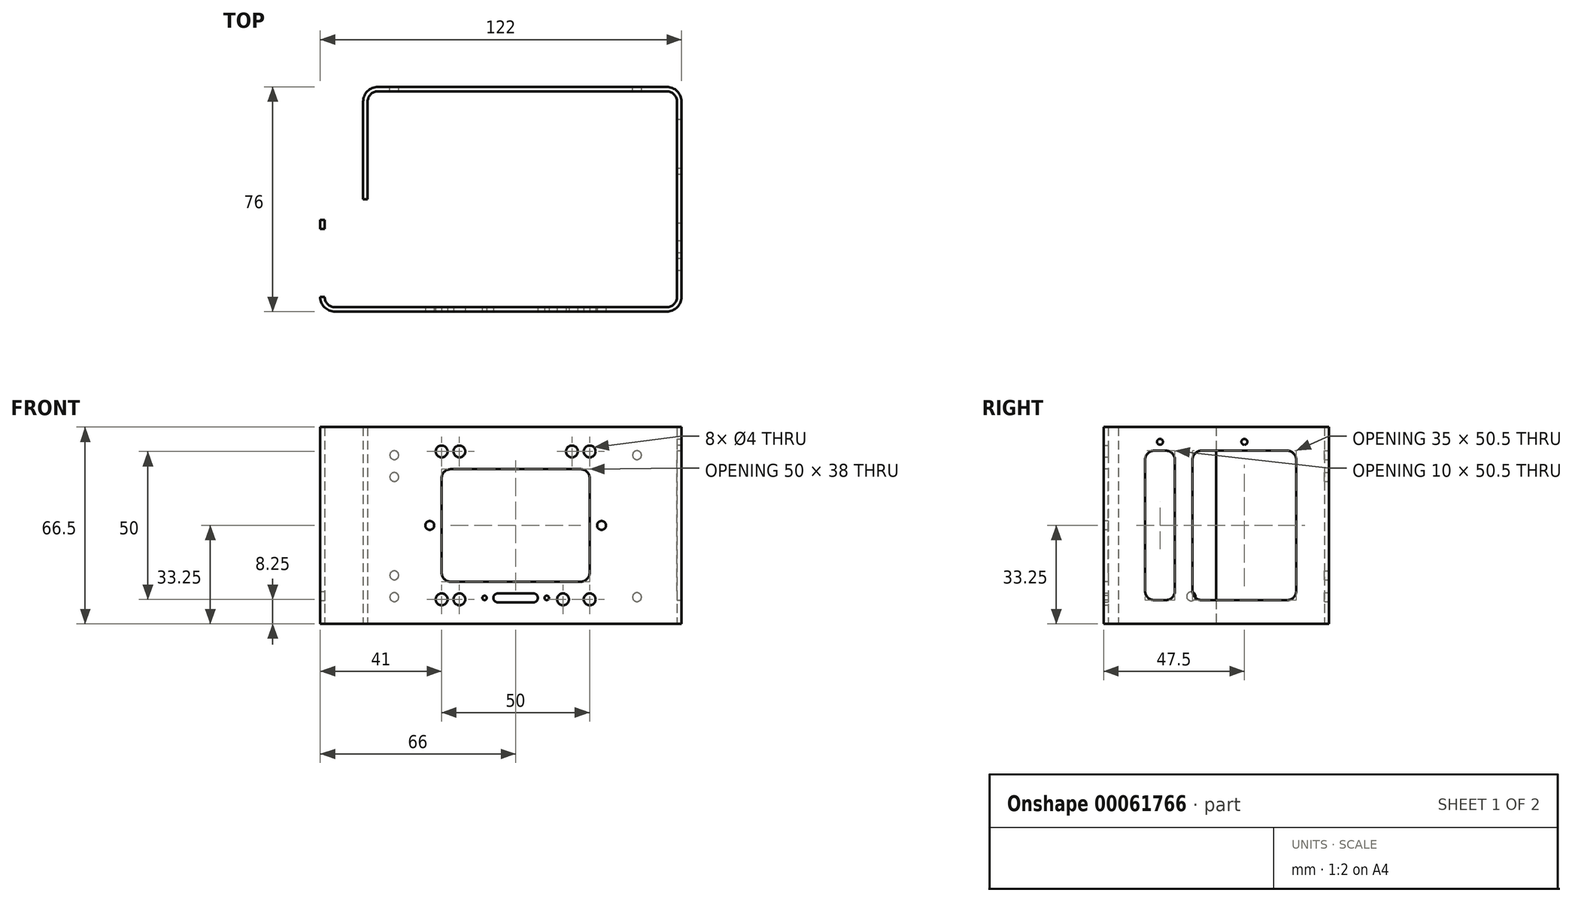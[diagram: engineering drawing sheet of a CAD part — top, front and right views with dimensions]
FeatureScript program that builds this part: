
annotation { "Feature Type Name" : "Feature", "Feature Type Description" : "" }
export const myFeature = defineFeature(function(context is Context, id is Id, definition is map)
    precondition{}
    {
        {
            var Q0;
            Q0=qCreatedBy(makeId("Top.planeOp"),FACE);
            var sketch = newSketch(context, id + "F0", { "sketchPlane" : qUnion([Q0])});
            skLineSegment(sketch, "E0", {"start": v(-64.5, 33) * mm, "end": v(-64.5, -33) * mm});
            skLineSegment(sketch, "E1", {"start": v(-61, -36.5) * mm, "end": v(51, -36.5) * mm});
            skLineSegment(sketch, "E2", {"start": v(54.5, -33) * mm, "end": v(54.5, 33) * mm});
            skLineSegment(sketch, "E3", {"start": v(51, 36.5) * mm, "end": v(-46.5, 36.5) * mm});
            skLineSegment(sketch, "E4", {"start": v(-50, 33) * mm, "end": v(-50, 0) * mm});
            skLineSegment(sketch, "E5.0", {"start": v(-51.5, 33) * mm, "end": v(-51.5, 0) * mm});
            skLineSegment(sketch, "E5.1", {"start": v(-66, 33) * mm, "end": v(-66, -33) * mm});
            skLineSegment(sketch, "E5.2", {"start": v(-61, -38) * mm, "end": v(51, -38) * mm});
            skLineSegment(sketch, "E5.3", {"start": v(56, -33) * mm, "end": v(56, 33) * mm});
            skLineSegment(sketch, "E5.4", {"start": v(51, 38) * mm, "end": v(-46.5, 38) * mm});
            skLineSegment(sketch, "E6", {"start": v(-50, 0) * mm, "end": v(-51.5, 0) * mm});
            skLineSegment(sketch, "E7", {"start": v(-64.5, 33) * mm, "end": v(-66, 33) * mm});
            skPoint(sketch, "E8.visualSharp", {"position": v(-64.5, -36.5) * mm});
            skArc(sketch, "E8.filletArc", {"start": v(-64.5, -33) * mm, "mid": v(-63.47, -35.47) * mm, "end": v(-61, -36.5) * mm});
            skPoint(sketch, "E9.visualSharp", {"position": v(54.5, -36.5) * mm});
            skArc(sketch, "E9.filletArc", {"start": v(51, -36.5) * mm, "mid": v(53.47, -35.47) * mm, "end": v(54.5, -33) * mm});
            skPoint(sketch, "E10.visualSharp", {"position": v(54.5, 36.5) * mm});
            skArc(sketch, "E10.filletArc", {"start": v(54.5, 33) * mm, "mid": v(53.47, 35.47) * mm, "end": v(51, 36.5) * mm});
            skPoint(sketch, "E11.visualSharp", {"position": v(-50, 36.5) * mm});
            skArc(sketch, "E11.filletArc", {"start": v(-46.5, 36.5) * mm, "mid": v(-48.97, 35.47) * mm, "end": v(-50, 33) * mm});
            skPoint(sketch, "E12.visualSharp", {"position": v(-66, -38) * mm});
            skArc(sketch, "E12.filletArc", {"start": v(-66, -33) * mm, "mid": v(-64.54, -36.54) * mm, "end": v(-61, -38) * mm});
            skPoint(sketch, "E13.visualSharp", {"position": v(56, -38) * mm});
            skArc(sketch, "E13.filletArc", {"start": v(51, -38) * mm, "mid": v(54.54, -36.54) * mm, "end": v(56, -33) * mm});
            skPoint(sketch, "E14.visualSharp", {"position": v(56, 38) * mm});
            skArc(sketch, "E14.filletArc", {"start": v(56, 33) * mm, "mid": v(54.54, 36.54) * mm, "end": v(51, 38) * mm});
            skPoint(sketch, "E15.visualSharp", {"position": v(-51.5, 38) * mm});
            skArc(sketch, "E15.filletArc", {"start": v(-46.5, 38) * mm, "mid": v(-50.04, 36.54) * mm, "end": v(-51.5, 33) * mm});
            skLineSegment(sketch, "E16", {"start": v(54.5, 0) * mm, "end": v(-12.48, 0) * mm, "construction": true});
            skLineSegment(sketch, "E17", {"start": v(2.25, 36.5) * mm, "end": v(-0.93, -15.16) * mm, "construction": true});
            skSolve(sketch);
        }
        {
            var Q0;
            Q0=qSketchRegion(id+"F0",true);
            extrude(context, id + "F1", {"entities" : qUnion([Q0]), "depth" : 66.5 * mm});
        }
        {
            var Q0;
            Q0=makeQuery(id+"F1.opExtrude","SWEPT_FACE",FACE,{"disambiguationData":[OSD([sQuery(id+"F0.wireOp",EDGE,"E5.2")])]});
            var sketch = newSketch(context, id + "F2", { "sketchPlane" : qUnion([Q0])});
            skLineSegment(sketch, "E18.bottom", {"start": v(-22, 52.25) * mm, "end": v(22, 52.25) * mm});
            skLineSegment(sketch, "E18.top", {"start": v(-22, 14.25) * mm, "end": v(22, 14.25) * mm});
            skLineSegment(sketch, "E18.left", {"start": v(-25, 49.25) * mm, "end": v(-25, 17.25) * mm});
            skLineSegment(sketch, "E18.right", {"start": v(25, 49.25) * mm, "end": v(25, 17.25) * mm});
            skLineSegment(sketch, "E19", {"start": v(-61, 33.25) * mm, "end": v(46, 33.25) * mm, "construction": true});
            skLineSegment(sketch, "E20", {"start": v(25, 33.25) * mm, "end": v(-25, 33.25) * mm, "construction": true});
            skPoint(sketch, "E21.visualSharp", {"position": v(-25, 52.25) * mm});
            skArc(sketch, "E21.filletArc", {"start": v(-22, 52.25) * mm, "mid": v(-24.12, 51.37) * mm, "end": v(-25, 49.25) * mm});
            skPoint(sketch, "E22.visualSharp", {"position": v(25, 52.25) * mm});
            skArc(sketch, "E22.filletArc", {"start": v(25, 49.25) * mm, "mid": v(24.12, 51.37) * mm, "end": v(22, 52.25) * mm});
            skPoint(sketch, "E23.visualSharp", {"position": v(25, 14.25) * mm});
            skArc(sketch, "E23.filletArc", {"start": v(22, 14.25) * mm, "mid": v(24.12, 15.13) * mm, "end": v(25, 17.25) * mm});
            skPoint(sketch, "E24.visualSharp", {"position": v(-25, 14.25) * mm});
            skArc(sketch, "E24.filletArc", {"start": v(-25, 17.25) * mm, "mid": v(-24.12, 15.13) * mm, "end": v(-22, 14.25) * mm});
            skCircle(sketch, "E25", {"center": v(-29, 33.25) * mm, "radius": 1.5 * mm});
            skCircle(sketch, "E26.MirrorC", {"center": v(29, 33.25) * mm, "radius": 1.5 * mm});
            skCircle(sketch, "E27", {"center": v(-25, 58.25) * mm, "radius": 2 * mm});
            skCircle(sketch, "E28.MirrorC", {"center": v(25, 58.25) * mm, "radius": 2 * mm});
            skCircle(sketch, "E29.MirrorC", {"center": v(-25, 8.25) * mm, "radius": 2 * mm});
            skCircle(sketch, "E30.MirrorC", {"center": v(25, 8.25) * mm, "radius": 2 * mm});
            skLineSegment(sketch, "E31.bottom", {"start": v(-6, 7.25) * mm, "end": v(6, 7.25) * mm});
            skPoint(sketch, "E32.visualSharp", {"position": v(7.5, 10.25) * mm});
            skLineSegment(sketch, "E31.top", {"start": v(-6, 10.25) * mm, "end": v(6, 10.25) * mm});
            skArc(sketch, "E33.filletArc", {"start": v(-6, 10.25) * mm, "mid": v(-7.06, 9.81) * mm, "end": v(-7.5, 8.75) * mm});
            skLineSegment(sketch, "E31.left", {"start": v(-7.5, 8.75) * mm, "end": v(-7.5, 8.75) * mm});
            skLineSegment(sketch, "E31.right", {"start": v(7.5, 8.75) * mm, "end": v(7.5, 8.75) * mm});
            skArc(sketch, "E34.filletArc", {"start": v(-7.5, 8.75) * mm, "mid": v(-7.06, 7.69) * mm, "end": v(-6, 7.25) * mm});
            skArc(sketch, "E35.filletArc", {"start": v(6, 7.25) * mm, "mid": v(7.06, 7.69) * mm, "end": v(7.5, 8.75) * mm});
            skArc(sketch, "E32.filletArc", {"start": v(7.5, 8.75) * mm, "mid": v(7.06, 9.81) * mm, "end": v(6, 10.25) * mm});
            skCircle(sketch, "E36", {"center": v(-10.5, 8.75) * mm, "radius": 0.75 * mm});
            skPoint(sketch, "E37", {"position": v(0, 10.25) * mm});
            skLineSegment(sketch, "E38", {"start": v(-10.5, 8.75) * mm, "end": v(8.14, 8.75) * mm, "construction": true});
            skPoint(sketch, "E33.visualSharp", {"position": v(-7.5, 10.25) * mm});
            skPoint(sketch, "E34.visualSharp", {"position": v(-7.5, 7.25) * mm});
            skPoint(sketch, "E35.visualSharp", {"position": v(7.5, 7.25) * mm});
            skLineSegment(sketch, "E39", {"start": v(0, 10.25) * mm, "end": v(0, 7.25) * mm, "construction": true});
            skCircle(sketch, "E40.MirrorC", {"center": v(10.5, 8.75) * mm, "radius": 0.75 * mm});
            skLineSegment(sketch, "E41", {"start": v(-25, 8.25) * mm, "end": v(-25, 58.25) * mm, "construction": true});
            skLineSegment(sketch, "E42", {"start": v(25, 58.25) * mm, "end": v(25, 8.25) * mm, "construction": true});
            skLineSegment(sketch, "E43", {"start": v(-25, 8.25) * mm, "end": v(25, 8.25) * mm, "construction": true});
            skLineSegment(sketch, "E44", {"start": v(25, 58.25) * mm, "end": v(-25, 58.25) * mm, "construction": true});
            skCircle(sketch, "E45", {"center": v(-19, 8.25) * mm, "radius": 2 * mm});
            skCircle(sketch, "E46.MirrorC", {"center": v(-19, 58.25) * mm, "radius": 2 * mm});
            skCircle(sketch, "E47.MirrorC", {"center": v(19, 58.25) * mm, "radius": 2 * mm});
            skCircle(sketch, "E48", {"center": v(16, 8.25) * mm, "radius": 2 * mm});
            skPoint(sketch, "E49", {"position": v(-61, 33.25) * mm});
            skSolve(sketch);
        }
        {
            var Q0;
            Q0 = qSketchRegion(id + "F2", true);
            extrude(context, id + "F3", {"entities" : qUnion([Q0]), "operationType" : NewBodyOperationType.REMOVE, "oppositeDirection" : true, "depth" : 25 * mm});
        }
        {
            var Q0;
            Q0=makeQuery(id+"F1.opExtrude","SWEPT_FACE",FACE,{"disambiguationData":[OSD([sQuery(id+"F0.wireOp",EDGE,"E5.4")])]});
            var sketch = newSketch(context, id + "F4", { "sketchPlane" : qUnion([Q0])});
            skCircle(sketch, "E50", {"center": v(-41, 57) * mm, "radius": 1.5 * mm});
            skLineSegment(sketch, "E51", {"start": v(-41, 57) * mm, "end": v(-41, 9) * mm, "construction": true});
            skLineSegment(sketch, "E52", {"start": v(-41, 9) * mm, "end": v(41, 9) * mm, "construction": true});
            skLineSegment(sketch, "E53", {"start": v(41, 9) * mm, "end": v(41, 57) * mm, "construction": true});
            skLineSegment(sketch, "E54", {"start": v(41, 57) * mm, "end": v(-41, 57) * mm, "construction": true});
            skCircle(sketch, "E55", {"center": v(-41, 9) * mm, "radius": 1.5 * mm});
            skCircle(sketch, "E56", {"center": v(41, 9) * mm, "radius": 1.5 * mm});
            skCircle(sketch, "E57", {"center": v(41, 57) * mm, "radius": 1.5 * mm});
            skLineSegment(sketch, "E58", {"start": v(0, 1) * mm, "end": v(0, 113) * mm, "construction": true});
            skPoint(sketch, "E58.endSnap0", {"position": v(0, 1) * mm});
            skPoint(sketch, "E59", {"position": v(0, 57) * mm});
            skCircle(sketch, "E60", {"center": v(41, 49.63) * mm, "radius": 1.5 * mm});
            skCircle(sketch, "E61", {"center": v(41, 16.38) * mm, "radius": 1.5 * mm});
            skLineSegment(sketch, "E62", {"start": v(33.74, 33) * mm, "end": v(24.94, 33) * mm, "construction": true});
            skSolve(sketch);
        }
        {
            var Q0;
            Q0=makeQuery(id+"F4.imprint","IMPRINT",FACE,{"disambiguationData":[TD([[makeQuery(id+"F4.imprint","IMPRINT",EDGE,{"derivedFrom":sQuery(id+"F4.wireOp",EDGE,"E50")}),1.0]])]});
            var Q1;
            Q1=makeQuery(id+"F4.imprint","IMPRINT",FACE,{"disambiguationData":[TD([[makeQuery(id+"F4.imprint","IMPRINT",EDGE,{"derivedFrom":sQuery(id+"F4.wireOp",EDGE,"E55")}),1.0]])]});
            var Q2;
            Q2=makeQuery(id+"F4.imprint","IMPRINT",FACE,{"disambiguationData":[TD([[makeQuery(id+"F4.imprint","IMPRINT",EDGE,{"derivedFrom":sQuery(id+"F4.wireOp",EDGE,"E56")}),1.0]])]});
            var Q3;
            Q3=makeQuery(id+"F4.imprint","IMPRINT",FACE,{"disambiguationData":[TD([[makeQuery(id+"F4.imprint","IMPRINT",EDGE,{"derivedFrom":sQuery(id+"F4.wireOp",EDGE,"E57")}),1.0]])]});
            var Q4;
            Q4=makeQuery(id+"F4.imprint","IMPRINT",FACE,{"disambiguationData":[TD([[makeQuery(id+"F4.imprint","IMPRINT",EDGE,{"derivedFrom":sQuery(id+"F4.wireOp",EDGE,"E61")}),1.0]])]});
            var Q5;
            Q5=makeQuery(id+"F4.imprint","IMPRINT",FACE,{"disambiguationData":[TD([[makeQuery(id+"F4.imprint","IMPRINT",EDGE,{"derivedFrom":sQuery(id+"F4.wireOp",EDGE,"E60")}),1.0]])]});
            extrude(context, id + "F5", {"entities" : qUnion([Q0, Q1, Q2, Q3, Q4, Q5]), "operationType" : NewBodyOperationType.REMOVE, "oppositeDirection" : true, "depth" : 25 * mm});
        }
        {
            var Q0;
            Q0=makeQuery(id+"F1.opExtrude","SWEPT_FACE",FACE,{"disambiguationData":[OSD([sQuery(id+"F0.wireOp",EDGE,"E5.3")])]});
            var sketch = newSketch(context, id + "F6", { "sketchPlane" : qUnion([Q0])});
            skLineSegment(sketch, "E63.bottom", {"start": v(-21, 58.5) * mm, "end": v(-17, 58.5) * mm});
            skLineSegment(sketch, "E63.top", {"start": v(-21, 8) * mm, "end": v(-17, 8) * mm});
            skLineSegment(sketch, "E63.left", {"start": v(-24, 55.5) * mm, "end": v(-24, 11) * mm});
            skLineSegment(sketch, "E63.right", {"start": v(-14, 55.5) * mm, "end": v(-14, 11) * mm});
            skLineSegment(sketch, "E64.bottom", {"start": v(-5, 58.5) * mm, "end": v(24, 58.5) * mm});
            skLineSegment(sketch, "E64.top", {"start": v(-5, 8) * mm, "end": v(24, 8) * mm});
            skLineSegment(sketch, "E64.left", {"start": v(-8, 55.5) * mm, "end": v(-8, 11) * mm});
            skLineSegment(sketch, "E64.right", {"start": v(27, 55.5) * mm, "end": v(27, 11) * mm});
            skLineSegment(sketch, "E65", {"start": v(-14, 58.5) * mm, "end": v(-8, 58.5) * mm, "construction": true});
            skLineSegment(sketch, "E66", {"start": v(-14, 8) * mm, "end": v(-8, 8) * mm, "construction": true});
            skPoint(sketch, "E67.visualSharp", {"position": v(-24, 58.5) * mm});
            skArc(sketch, "E67.filletArc", {"start": v(-21, 58.5) * mm, "mid": v(-23.12, 57.62) * mm, "end": v(-24, 55.5) * mm});
            skPoint(sketch, "E68.visualSharp", {"position": v(-14, 58.5) * mm});
            skArc(sketch, "E68.filletArc", {"start": v(-14, 55.5) * mm, "mid": v(-14.88, 57.62) * mm, "end": v(-17, 58.5) * mm});
            skPoint(sketch, "E69.visualSharp", {"position": v(-24, 8) * mm});
            skArc(sketch, "E69.filletArc", {"start": v(-24, 11) * mm, "mid": v(-23.12, 8.88) * mm, "end": v(-21, 8) * mm});
            skPoint(sketch, "E70.visualSharp", {"position": v(-14, 8) * mm});
            skArc(sketch, "E70.filletArc", {"start": v(-17, 8) * mm, "mid": v(-14.88, 8.88) * mm, "end": v(-14, 11) * mm});
            skPoint(sketch, "E71.visualSharp", {"position": v(-8, 8) * mm});
            skArc(sketch, "E71.filletArc", {"start": v(-8, 11) * mm, "mid": v(-7.12, 8.88) * mm, "end": v(-5, 8) * mm});
            skPoint(sketch, "E72.visualSharp", {"position": v(27, 8) * mm});
            skArc(sketch, "E72.filletArc", {"start": v(24, 8) * mm, "mid": v(26.12, 8.88) * mm, "end": v(27, 11) * mm});
            skPoint(sketch, "E73.visualSharp", {"position": v(27, 58.5) * mm});
            skArc(sketch, "E73.filletArc", {"start": v(27, 55.5) * mm, "mid": v(26.12, 57.62) * mm, "end": v(24, 58.5) * mm});
            skPoint(sketch, "E74.visualSharp", {"position": v(-8, 58.5) * mm});
            skArc(sketch, "E74.filletArc", {"start": v(-5, 58.5) * mm, "mid": v(-7.12, 57.62) * mm, "end": v(-8, 55.5) * mm});
            skCircle(sketch, "E75", {"center": v(-19, 61.5) * mm, "radius": 1 * mm});
            skLineSegment(sketch, "E76", {"start": v(-24, 33.25) * mm, "end": v(27, 33.25) * mm, "construction": true});
            skLineSegment(sketch, "E77", {"start": v(-19, 58.5) * mm, "end": v(-19, 8) * mm, "construction": true});
            skPoint(sketch, "E77.endSnap0", {"position": v(-19, 8) * mm});
            skLineSegment(sketch, "E78", {"start": v(9.5, 8) * mm, "end": v(9.5, 58.5) * mm, "construction": true});
            skCircle(sketch, "E79", {"center": v(9.5, 61.5) * mm, "radius": 1 * mm});
            skCircle(sketch, "E80.MirrorC", {"center": v(-19, 5) * mm, "radius": 1 * mm});
            skCircle(sketch, "E81.MirrorC", {"center": v(9.5, 5) * mm, "radius": 1 * mm});
            skSolve(sketch);
        }
        {
            var Q0;
            Q0=makeQuery(id+"F6.imprint","IMPRINT",FACE,{"disambiguationData":[TD([[makeQuery(id+"F6.imprint","IMPRINT",EDGE,{"derivedFrom":sQuery(id+"F6.wireOp",EDGE,"E63.bottom")}),-1.0]])]});
            var Q1;
            Q1=makeQuery(id+"F6.imprint","IMPRINT",FACE,{"disambiguationData":[TD([[makeQuery(id+"F6.imprint","IMPRINT",EDGE,{"derivedFrom":sQuery(id+"F6.wireOp",EDGE,"E64.bottom")}),-1.0]])]});
            var Q2;
            Q2=makeQuery(id+"F6.imprint","IMPRINT",FACE,{"disambiguationData":[TD([[makeQuery(id+"F6.imprint","IMPRINT",EDGE,{"derivedFrom":sQuery(id+"F6.wireOp",EDGE,"E63.bottom")}),-1.0]])]});
            var Q3;
            Q3=makeQuery(id+"F6.imprint","IMPRINT",FACE,{"disambiguationData":[TD([[makeQuery(id+"F6.imprint","IMPRINT",EDGE,{"derivedFrom":sQuery(id+"F6.wireOp",EDGE,"E64.bottom")}),-1.0]])]});
            var Q4;
            Q4=makeQuery(id+"F6.imprint","IMPRINT",FACE,{"disambiguationData":[TD([[makeQuery(id+"F6.imprint","IMPRINT",EDGE,{"derivedFrom":sQuery(id+"F6.wireOp",EDGE,"E75")}),1.0]])]});
            var Q5;
            Q5=makeQuery(id+"F6.imprint","IMPRINT",FACE,{"disambiguationData":[TD([[makeQuery(id+"F6.imprint","IMPRINT",EDGE,{"derivedFrom":sQuery(id+"F6.wireOp",EDGE,"E79")}),1.0]])]});
            var Q6;
            Q6=makeQuery(id+"F6.imprint","IMPRINT",FACE,{"disambiguationData":[TD([[makeQuery(id+"F6.imprint","IMPRINT",EDGE,{"derivedFrom":sQuery(id+"F6.wireOp",EDGE,"E81.MirrorC")}),-1.0]])]});
            var Q7;
            Q7=makeQuery(id+"F6.imprint","IMPRINT",FACE,{"disambiguationData":[TD([[makeQuery(id+"F6.imprint","IMPRINT",EDGE,{"derivedFrom":sQuery(id+"F6.wireOp",EDGE,"E80.MirrorC")}),-1.0]])]});
            extrude(context, id + "F7", {"entities" : qUnion([Q0, Q1, Q2, Q3, Q4, Q5, Q6, Q7]), "operationType" : NewBodyOperationType.REMOVE, "oppositeDirection" : true, "depth" : 25 * mm});
        }
        {
            var Q0;
            Q0=makeQuery(id+"F1.opExtrude","SWEPT_FACE",FACE,{"disambiguationData":[OSD([sQuery(id+"F0.wireOp",EDGE,"E5.1")])]});
            var sketch = newSketch(context, id + "F8", { "sketchPlane" : qUnion([Q0])});
            skLineSegment(sketch, "E82", {"start": v(8.5, 66.5) * mm, "end": v(8.5, 0) * mm, "construction": true});
            skLineSegment(sketch, "E83.0.0", {"start": v(-33, 0) * mm, "end": v(33, 0) * mm});
            skLineSegment(sketch, "E83.0.1", {"start": v(33, 0) * mm, "end": v(33, 66.5) * mm});
            skLineSegment(sketch, "E83.0.2", {"start": v(33, 66.5) * mm, "end": v(-33, 66.5) * mm});
            skLineSegment(sketch, "E83.0.3", {"start": v(-33, 66.5) * mm, "end": v(-33, 0) * mm});
            skLineSegment(sketch, "E84", {"start": v(-33, 33.25) * mm, "end": v(33, 33.25) * mm, "construction": true});
            skCircle(sketch, "E85", {"center": v(8.5, 57.25) * mm, "radius": 1.5 * mm});
            skCircle(sketch, "E86.MirrorC", {"center": v(8.5, 9.25) * mm, "radius": 1.5 * mm});
            skSolve(sketch);
        }
        {
            var Q0;
            Q0=makeQuery(id+"F8.imprint","IMPRINT",FACE,{"disambiguationData":[TD([[makeQuery(id+"F8.imprint","IMPRINT",EDGE,{"derivedFrom":sQuery(id+"F8.wireOp",EDGE,"E85")}),1.0]])]});
            var Q1;
            Q1=makeQuery(id+"F8.imprint","IMPRINT",FACE,{"disambiguationData":[TD([[makeQuery(id+"F8.imprint","IMPRINT",EDGE,{"derivedFrom":sQuery(id+"F8.wireOp",EDGE,"E86.MirrorC")}),-1.0]])]});
            extrude(context, id + "F9", {"entities" : qUnion([Q0, Q1]), "operationType" : NewBodyOperationType.REMOVE, "oppositeDirection" : true, "depth" : 1.5 * mm});
        }
    });
